# Revit family: Kessel 730200.10XR en
name_source: partatom
category: Sanitärinstallationen
revit_build: Autodesk Revit 2017 (Build: 20160225_1515(x64)
units: mm (PartAtom-declared; Revit-internal decimal feet)

## family parameters
Arbeitsebenenbasiert = Nein
Beim Laden mit Abzugskörper schneiden = Nein
Bemaßung runder Anschluss = Durchmesser verwenden
Gemeinsam genutzt = Nein
Immer vertikal = Ja
Raumberechnungspunkt = Nein
Teiletyp = Normal

## types (1)
- Kessel 730200.10XR en
    <1.010.00.2> Number of the part of the guideline = 38
    <1.010.00.3> Issue date (month) of the guideline = 201805
    <1.010.00.4> Manufacturer name = Kessel
    <1.010.00.5> Revision date of the file = 20190228
    <1.800.00.3> BS number = 10000500000000000000000000000300000000200000000029???00001
    <1.800.00.4> Comment field = Rückstauverschluss Staufix DN 200, Bodenplatte, befliesbar, Typ 2 R
    <1.810.00.3> Manufacturer’s reference number = 730200.10XR
    <1.810.00.4> DATANORM number = 730200.10XR
    <1.810.00.6> GTIN number = 4026092076576
    <1.960/3L.00.8> Link (URL) = http://www.kessel.de
    <38.100.00.4> Drain type for floor, roof and sanitary objects = Rückstauverschlüsse
    <38.110.00.4> Floor, roof and sanitary works sequences = Rückstauverschluss Staufix
    <38.400.00.3> Material of the drain body = Kunststoff
    <38.500.00.3> Sealing variantion = mit Klebeflansch
    <38.700.00.15> Connection to GLT, GA = no
    <38.700.00.16> Fire resistance class can be retrofitted = no
    <38.700.00.4> product name = Rückstauverschluss Staufix DN 200, Bodenplatte, befliesbar, Typ 2 R
    <38.700.00.6> Complete article (one-piece) from combination (multi-part design) Drain body and attachment piece = yes
    <38.700.00.7> Potential compensation (ground connection) available = no
    <38.700.00.8> Electrical connection = no
    <38.710.01.10> depth [mm] = 444
    <38.710.01.14> with sound decoupling = no
    <38.710.01.15> Leafy / Kiefang = no
    <38.710.01.3> Product name = Rückstauverschluss Staufix DN 200, Bodenplatte, befliesbar, Typ 2 R
    <38.710.01.4> Type = other
    <38.710.01.5> Nominal system = DN
    <38.710.01.6> Nominal dimensions = 200
    <38.710.01.9> installation width [mm] = 586
    <38.710.13.3> Product name = Rückstauverschluss Staufix DN 200, Bodenplatte, befliesbar, Typ 2 R
    <38.710.13.4> Variant of the drainage drain = point drain
    <38.710.13.7> Leafy / Kiefang = no
    <38.710.15.3> Product name = befliesbare Abdeckplatte, Kunststoff
    <38.710.15.4> Execution drain grate = befliesbare Abdeckplatte
    <38.710.15.5> Material of the drain grate = plastic
    <38.710.15.6> Fixing the grate = lockable
    <38.710.15.7> Execution of the drain grate = befliesbare Abdeckplatte
    <38.710.15.9> Slip resistance of the drain grate = no
    <38.710.16.3> Type of measurements = external dimensions
    <38.710.16.4> Length = 586
    <38.710.16.5> Width = 444
    CONNECTOR0_DIAMETER_dX_0r = 0 mm  [stored 0 ft]
    CONNECTOR0_dX_01 = 20 mm
    CONNECTOR0_ref_dX = 20 mm
    CONNECTOR0_ref_dZ = 21 mm
    CONNECTOR1_DIAMETER_dX_0r = 0 mm  [stored 0 ft]
    CONNECTOR1_dX_00 = 496 mm
    CONNECTOR1_dX_01 = 586 mm
    CONNECTOR1_ref_dX = 496 mm
    CONNECTOR1_ref_dZ = 13 mm
    Hersteller = Kessel
    Modell = 730200.10XR
    URL = www.kessel.de

note: [stored X ft] marks values corroborated as IEEE doubles in the binary element streams (Revit-internal decimal feet)

## geometry (parser evidence)
native form markers: Sweep x1
no freeform markers — native parametric forms only
